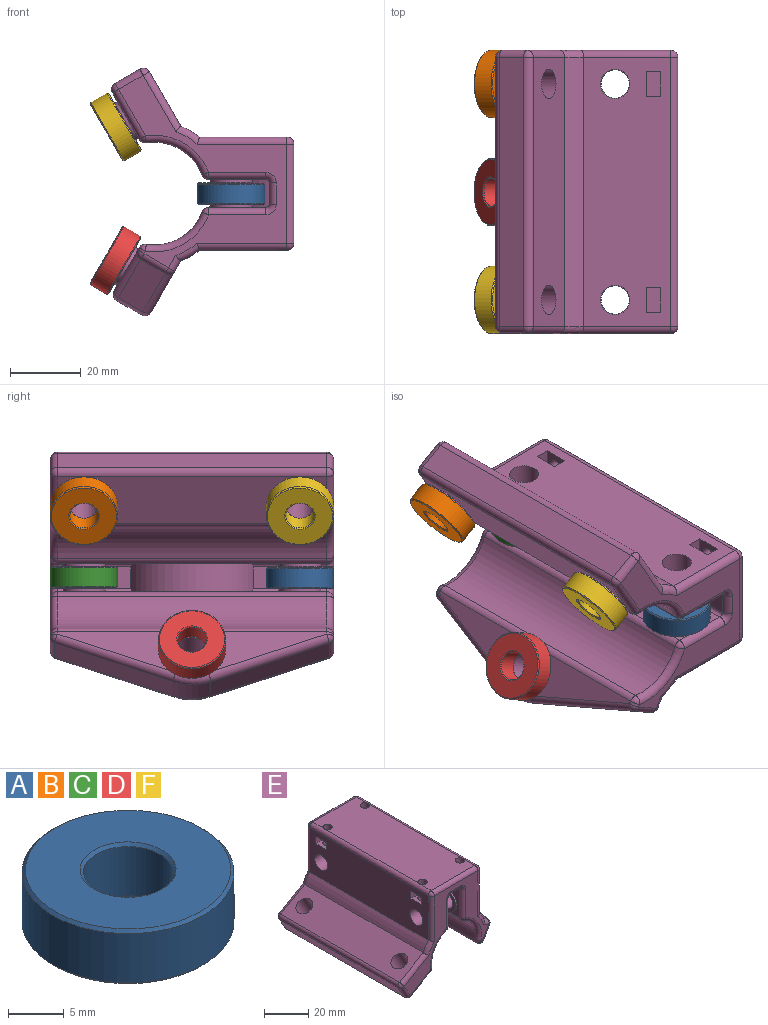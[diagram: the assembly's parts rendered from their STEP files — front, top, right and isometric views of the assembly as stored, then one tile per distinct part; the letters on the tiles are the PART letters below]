
ASSEMBLY  parts=6 mates=5
PART A: 8 faces, bbox 19x19x6 mm
  f0: cylinder r=4mm len=8mm, axis (0,0,-1), area 135.7mm2, adj f4,f6
  f1: cylinder r=9.5mm len=19mm, axis (0,0,-1), area 322.3mm2, adj f5,f7
  f2: plane 18.4x18.4mm, normal (0,0,1), area 207.8mm2, adj f6,f7
  f3: plane 18.4x18.4mm, normal (0,0,-1), area 207.8mm2, adj f4,f5
  f4: cone r=4.3mm half-angle=45deg, axis (0,0,-1), area 11.1mm2, adj f0,f3
  f5: cone r=9.5mm half-angle=45deg, axis (0,0,1), area 24.9mm2, adj f1,f3
  f6: cone r=4mm half-angle=45deg, axis (0,0,1), area 11.1mm2, adj f0,f2
  f7: cone r=9.2mm half-angle=45deg, axis (0,0,-1), area 24.9mm2, adj f1,f2
PART B: same geometry as A
PART C: same geometry as A
PART D: same geometry as A
PART E: 155 faces, bbox 70.9x80x51.6 mm
  f0: plane 54.37x47.54mm, normal (0,1,0), area 620.3mm2, adj f104,f108,f112,f114,f115,f117,f118,f119
  f1: plane 54.37x47.54mm, normal (0,-1,0), area 620.3mm2, adj f83,f84,f86,f87,f88,f89,f90,f91
  f2: plane 76x28mm, normal (0,0,1), area 2071.7mm2, adj f67,f68,f71,f74,f97,f124,f144,f147
  f3: plane 76x24.66mm, normal (-1,0,0), area 1712.3mm2, adj f14,f24,f25,f55,f56,f57,f58,f60
  f4: plane 76x24.71mm, normal (1,0,0), area 1716.4mm2, adj f13,f22,f23,f45,f46,f47,f48,f50
  f5: plane 20.76x6mm, normal (0,0,-1), area 124.5mm2, adj f6,f31,f32,f88
  f6: cylinder r=1mm len=21.18mm, axis (0,-1,0), area 32.8mm2, adj f5,f8,f32,f90
  f7: cylinder r=1mm len=21.18mm, axis (0,1,0), area 32.8mm2, adj f9,f17,f32,f119
  f8: plane 76x16.13mm, normal (1,0,0), area 738.4mm2, adj f6,f27,f30,f32,f41,f43,f92,f112
  f9: plane 76x16.13mm, normal (-1,0,0), area 738.4mm2, adj f7,f28,f31,f32,f37,f39,f84,f121
  f10: plane 76x15.34mm, normal (-0.5,0,0.87), area 1240.4mm2, adj f14,f20,f21,f105,f113,f118
  f11: plane 76x13.11mm, normal (0.5,0,-0.87), area 924.3mm2, adj f26,f33,f35,f100,f107,f108
  f12: plane 76x14.41mm, normal (0.5,0,0.87), area 734.6mm2, adj f13,f77,f91,f130,f134,f135,f136
  f13: cylinder r=20.5mm len=76mm, axis (0,1,0), area 472.9mm2, adj f4,f12,f93,f128
  f14: cylinder r=20.5mm len=76mm, axis (0,1,0), area 472.9mm2, adj f3,f10,f101,f120
  f15: plane 76x6.93mm, normal (-0.87,0,-0.5), area 608mm2, adj f106,f107,f113,f114
  f16: cylinder r=14.5mm len=76mm, axis (0,1,0), area 1486.2mm2, adj f26,f27,f96,f104
  f17: plane 20.76x6mm, normal (0,0,-1), area 124.5mm2, adj f7,f30,f32,f117
  f18: cylinder r=14.5mm len=76mm, axis (0,1,0), area 1489.3mm2, adj f28,f29,f83,f125
  f19: plane 76x12.21mm, normal (-0.5,0,-0.87), area 481.5mm2, adj f29,f78,f87,f129,f139,f140,f141
  f20: cylinder r=4.1mm len=15.36mm, axis (-0.5,0,0.87), area 334.9mm2, adj f10,f36
  f21: cylinder r=4.1mm len=15.36mm, axis (-0.5,0,0.87), area 334.9mm2, adj f10,f34
  f22: cylinder r=4.1mm len=12.85mm, axis (1,0,0), area 331mm2, adj f4,f40
  f23: cylinder r=4.1mm len=12.85mm, axis (1,0,0), area 331mm2, adj f4,f38
  f24: cylinder r=4.1mm len=12.85mm, axis (1,0,0), area 331mm2, adj f3,f44
  f25: cylinder r=4.1mm len=12.85mm, axis (1,0,0), area 331mm2, adj f3,f42
  f26: cylinder r=2mm len=76mm, axis (0,1,0), area 182mm2, adj f11,f16,f98,f103
  f27: cylinder r=2mm len=76mm, axis (0,1,0), area 182.2mm2, adj f8,f16,f94,f109
  f28: cylinder r=2mm len=76mm, axis (0,1,0), area 182.2mm2, adj f9,f18,f82,f123
  f29: cylinder r=2mm len=76mm, axis (0,1,0), area 182.4mm2, adj f18,f19,f85,f127
  f30: cylinder r=1mm len=21.18mm, axis (0,-1,0), area 32.8mm2, adj f8,f17,f32,f115
  f31: cylinder r=1mm len=21.18mm, axis (0,1,0), area 32.8mm2, adj f5,f9,f32,f86
  f32: cylinder r=18.5mm len=34.49mm, axis (1,0,0), area 354.4mm2, adj f5,f6,f7,f8,f9,f17,f30,f31
  f33: cylinder r=6mm len=12mm, axis (-0.5,0,0.87), area 37.7mm2, adj f11,f34
  f34: plane 12x10.39mm, normal (0.5,0,-0.87), area 60.3mm2, adj f21,f33
  f35: cylinder r=6mm len=12mm, axis (-0.5,0,0.87), area 37.7mm2, adj f11,f36
  f36: plane 12x10.39mm, normal (0.5,0,-0.87), area 60.3mm2, adj f20,f35
  f37: cylinder r=6mm len=12mm, axis (1,0,0), area 31.2mm2, adj f9,f38
  f38: plane 12x12mm, normal (-1,0,0), area 60.3mm2, adj f23,f37
  f39: cylinder r=6mm len=12mm, axis (1,0,0), area 31.2mm2, adj f9,f40
  f40: plane 12x12mm, normal (-1,0,0), area 60.3mm2, adj f22,f39
  f41: cylinder r=6mm len=12mm, axis (-1,0,0), area 32.9mm2, adj f8,f42
  f42: plane 12x12mm, normal (1,0,0), area 60.3mm2, adj f25,f41
  f43: cylinder r=6mm len=12mm, axis (-1,0,0), area 32.9mm2, adj f8,f44
  f44: plane 12x12mm, normal (1,0,0), area 60.3mm2, adj f24,f43
  f45: plane 8x4mm, normal (0,1,0), area 32mm2, adj f4,f46,f48,f49
  f46: plane 8x7mm, normal (0,0,1), area 41.8mm2, adj f4,f45,f47,f49,f75
  f47: plane 8x4mm, normal (0,-1,0), area 32mm2, adj f4,f46,f48,f49
  f48: plane 8x7mm, normal (0,0,-1), area 41.8mm2, adj f4,f45,f47,f49,f74
  f49: plane 7x4mm, normal (1,0,0), area 28mm2, adj f45,f46,f47,f48
  f50: plane 8x7mm, normal (0,0,1), area 41.8mm2, adj f4,f51,f53,f54,f72
  f51: plane 8x4mm, normal (0,-1,0), area 32mm2, adj f4,f50,f52,f54
  f52: plane 8x7mm, normal (0,0,-1), area 41.8mm2, adj f4,f51,f53,f54,f71
  f53: plane 8x4mm, normal (0,1,0), area 32mm2, adj f4,f50,f52,f54
  f54: plane 7x4mm, normal (1,0,0), area 28mm2, adj f50,f51,f52,f53
  f55: plane 8x7mm, normal (0,0,1), area 41.8mm2, adj f3,f56,f58,f59,f69
  f56: plane 8x4mm, normal (0,1,0), area 32mm2, adj f3,f55,f57,f59
  f57: plane 8x7mm, normal (0,0,-1), area 41.8mm2, adj f3,f56,f58,f59,f68
  f58: plane 8x4mm, normal (0,-1,0), area 32mm2, adj f3,f55,f57,f59
  f59: plane 7x4mm, normal (-1,0,0), area 28mm2, adj f55,f56,f57,f58
  f60: plane 8x7mm, normal (0,0,-1), area 41.8mm2, adj f3,f61,f63,f64,f67
  f61: plane 8x4mm, normal (0,-1,0), area 32mm2, adj f3,f60,f62,f64
  f62: plane 8x7mm, normal (0,0,1), area 41.8mm2, adj f3,f61,f63,f64,f66
  f63: plane 8x4mm, normal (0,1,0), area 32mm2, adj f3,f60,f62,f64
  f64: plane 7x4mm, normal (-1,0,0), area 28mm2, adj f60,f61,f62,f63
  f65: plane 4.25x4.25mm, normal (0,0,1), area 14.2mm2, adj f66
  f66: cylinder r=2.12mm len=4.25mm, axis (0,0,1), area 53.4mm2, adj f62,f65
  f67: cylinder r=2.12mm len=5mm, axis (0,0,1), area 66.8mm2, adj f2,f60,f147
  f68: cylinder r=2.12mm len=5mm, axis (0,0,1), area 66.8mm2, adj f2,f57,f147
  f69: cylinder r=2.12mm len=4.25mm, axis (0,0,1), area 53.4mm2, adj f55,f70
  f70: plane 4.25x4.25mm, normal (0,0,1), area 14.2mm2, adj f69
  f71: cylinder r=2.12mm len=5mm, axis (0,0,1), area 66.8mm2, adj f2,f52,f144
  f72: cylinder r=2.12mm len=4.25mm, axis (0,0,1), area 53.4mm2, adj f50,f73
  f73: plane 4.25x4.25mm, normal (0,0,1), area 14.2mm2, adj f72
  f74: cylinder r=2.12mm len=5mm, axis (0,0,1), area 66.8mm2, adj f2,f48,f144
  f75: cylinder r=2.12mm len=4.25mm, axis (0,0,1), area 53.4mm2, adj f46,f76
  f76: plane 4.25x4.25mm, normal (0,0,1), area 14.2mm2, adj f75
  f77: cylinder r=4.1mm len=15.36mm, axis (0.5,0,0.87), area 334.9mm2, adj f12,f79
  f78: cylinder r=6mm len=12mm, axis (0.5,0,0.87), area 37.7mm2, adj f19,f79
  f79: plane 12x10.39mm, normal (-0.5,0,-0.87), area 60.3mm2, adj f77,f78
  f80: plane 33.44x14.86mm, normal (0.81,-0.35,-0.47), area 285.7mm2, adj f89,f132,f134,f139
  f81: plane 33.44x14.86mm, normal (0.81,0.35,-0.47), area 285.7mm2, adj f131,f132,f136,f141
  f82: sphere r=2mm, area 4.8mm2, adj f28,f83,f84
  f83: torus R=16.5mm, axis (0,-1,0), area 64.6mm2, adj f1,f18,f82,f85
  f84: cylinder r=2mm len=16.13mm, axis (0,0,1), area 50.7mm2, adj f1,f9,f82,f86
  f85: sphere r=2mm, area 4.8mm2, adj f29,f83,f87
  f86: torus R=3mm, axis (0,-1,0), area 8.5mm2, adj f1,f31,f84,f88
  f87: cylinder r=2mm len=2.1mm, axis (-0.87,0,0.5), area 2.3mm2, adj f1,f19,f85,f138
  f88: cylinder r=2mm len=6mm, axis (-1,0,0), area 18.8mm2, adj f1,f5,f86,f90
  f89: cylinder r=2mm len=7.86mm, axis (-0.5,0,-0.87), area 19.4mm2, adj f1,f80,f133,f138
  f90: torus R=3mm, axis (0,-1,0), area 8.5mm2, adj f1,f6,f88,f92
  f91: cylinder r=2mm len=4.46mm, axis (0.87,0,-0.5), area 11.1mm2, adj f1,f12,f93,f133
  f92: cylinder r=2mm len=16.13mm, axis (0,0,-1), area 50.7mm2, adj f1,f8,f90,f94
  f93: torus R=18.5mm, axis (0,-1,0), area 20.4mm2, adj f1,f13,f91,f95
  f94: sphere r=2mm, area 4.8mm2, adj f27,f92,f96
  f95: cylinder r=2mm len=25.43mm, axis (0,0,-1), area 78.4mm2, adj f1,f4,f93,f145
  f96: torus R=16.5mm, axis (0,-1,0), area 64.5mm2, adj f1,f16,f94,f98
  f97: cylinder r=2mm len=28mm, axis (1,0,0), area 88mm2, adj f1,f2,f145,f148
  f98: sphere r=2mm, area 4.8mm2, adj f26,f96,f100
  f99: cylinder r=2mm len=25.38mm, axis (0,0,1), area 78.3mm2, adj f1,f3,f101,f148
  f100: cylinder r=2mm len=14.11mm, axis (-0.87,0,-0.5), area 47.6mm2, adj f1,f11,f98,f102
  f101: torus R=18.5mm, axis (0,-1,0), area 20.4mm2, adj f1,f14,f99,f105
  f102: sphere r=2mm, area 6.3mm2, adj f100,f106,f107
  f103: sphere r=2mm, area 4.8mm2, adj f26,f104,f108
  f104: torus R=16.5mm, axis (0,-1,0), area 64.5mm2, adj f0,f16,f103,f109
  f105: cylinder r=2mm len=16.96mm, axis (0.87,0,0.5), area 56.5mm2, adj f1,f10,f101,f110
  f106: cylinder r=2mm len=7.93mm, axis (-0.5,0,0.87), area 25.1mm2, adj f1,f15,f102,f110
  f107: cylinder r=2mm len=76mm, axis (0,1,0), area 238.8mm2, adj f11,f15,f102,f111
  f108: cylinder r=2mm len=14.11mm, axis (0.87,0,0.5), area 47.6mm2, adj f0,f11,f103,f111
  f109: sphere r=2mm, area 4.8mm2, adj f27,f104,f112
  f110: sphere r=2mm, area 6.3mm2, adj f105,f106,f113
  f111: sphere r=2mm, area 6.3mm2, adj f107,f108,f114
  f112: cylinder r=2mm len=16.13mm, axis (0,0,1), area 50.7mm2, adj f0,f8,f109,f115
  f113: cylinder r=2mm len=76mm, axis (0,1,0), area 238.8mm2, adj f10,f15,f110,f116
  f114: cylinder r=2mm len=7.93mm, axis (0.5,0,-0.87), area 25.1mm2, adj f0,f15,f111,f116
  f115: torus R=3mm, axis (0,-1,0), area 8.5mm2, adj f0,f30,f112,f117
  f116: sphere r=2mm, area 6.3mm2, adj f113,f114,f118
  f117: cylinder r=2mm len=6mm, axis (1,0,0), area 18.8mm2, adj f0,f17,f115,f119
  f118: cylinder r=2mm len=16.96mm, axis (-0.87,0,-0.5), area 56.5mm2, adj f0,f10,f116,f120
  f119: torus R=3mm, axis (0,-1,0), area 8.5mm2, adj f0,f7,f117,f121
  f120: torus R=18.5mm, axis (0,-1,0), area 20.4mm2, adj f0,f14,f118,f122
  f121: cylinder r=2mm len=16.13mm, axis (0,0,-1), area 50.7mm2, adj f0,f9,f119,f123
  f122: cylinder r=2mm len=25.38mm, axis (0,0,-1), area 78.3mm2, adj f0,f3,f120,f146
  f123: sphere r=2mm, area 4.8mm2, adj f28,f121,f125
  f124: cylinder r=2mm len=28mm, axis (-1,0,0), area 88mm2, adj f0,f2,f143,f146
  f125: torus R=16.5mm, axis (0,-1,0), area 64.6mm2, adj f0,f18,f123,f127
  f126: cylinder r=2mm len=25.43mm, axis (0,0,1), area 78.4mm2, adj f0,f4,f128,f143
  f127: sphere r=2mm, area 4.8mm2, adj f29,f125,f129
  f128: torus R=18.5mm, axis (0,-1,0), area 20.4mm2, adj f0,f13,f126,f130
  f129: cylinder r=2mm len=2.1mm, axis (0.87,0,-0.5), area 2.3mm2, adj f0,f19,f127,f142
  f130: cylinder r=2mm len=4.46mm, axis (-0.87,0,0.5), area 11.1mm2, adj f0,f12,f128,f137
  f131: cylinder r=2mm len=7.86mm, axis (0.5,0,0.87), area 19.4mm2, adj f0,f81,f137,f142
  f132: cylinder r=15mm len=10.53mm, axis (0.5,0,0.87), area 86.1mm2, adj f80,f81,f135,f140
  f133: sphere r=2mm, area 4.8mm2, adj f89,f91,f134
  f134: cylinder r=2mm len=34.14mm, axis (0.3,0.94,-0.18), area 112.2mm2, adj f12,f80,f133,f135
  f135: torus R=13mm, axis (0.5,0,0.87), area 32.2mm2, adj f12,f132,f134,f136
  f136: cylinder r=2mm len=34.14mm, axis (-0.3,0.94,0.18), area 112.2mm2, adj f12,f81,f135,f137
  f137: sphere r=2mm, area 4.8mm2, adj f130,f131,f136
  f138: sphere r=2mm, area 4.8mm2, adj f87,f89,f139
  f139: cylinder r=2mm len=34.14mm, axis (-0.3,-0.94,0.18), area 112.2mm2, adj f19,f80,f138,f140
  f140: torus R=13mm, axis (0.5,0,0.87), area 32.2mm2, adj f19,f132,f139,f141
  f141: cylinder r=2mm len=34.14mm, axis (0.3,-0.94,-0.18), area 112.2mm2, adj f19,f81,f140,f142
  f142: sphere r=2mm, area 4.8mm2, adj f129,f131,f141
  f143: sphere r=2mm, area 6.3mm2, adj f124,f126,f144
  f144: cylinder r=2mm len=76mm, axis (0,1,0), area 238.5mm2, adj f2,f4,f71,f74,f143,f145
  f145: sphere r=2mm, area 6.3mm2, adj f95,f97,f144
  f146: sphere r=2mm, area 6.3mm2, adj f122,f124,f147
  f147: cylinder r=2mm len=76mm, axis (0,1,0), area 238.5mm2, adj f2,f3,f67,f68,f146,f148
  f148: sphere r=2mm, area 6.3mm2, adj f97,f99,f147
  f149: cylinder r=12.5mm len=21.11mm, axis (1,0,0), area 200mm2, adj f150,f151,f152,f153,f154
  f150: cylinder r=1mm len=21.11mm, axis (0,1,0), area 32.4mm2, adj f149,f152,f153
  f151: cylinder r=1mm len=21.11mm, axis (0,-1,0), area 32.4mm2, adj f149,f152,f154
  f152: plane 21.11x6mm, normal (0,0,-1), area 126.6mm2, adj f149,f150,f151
  f153: plane 19.7x4.8mm, normal (-1,0,0), area 66mm2, adj f149,f150
  f154: plane 19.7x4.8mm, normal (1,0,0), area 66mm2, adj f149,f151
PART F: same geometry as A
PLACE A t=(5.17,-67.56,12.38)mm
PLACE B rot(axis=(0,1,0),60deg) t=(-30.04,-6.56,32.9)mm
PLACE C t=(5.17,-6.56,12.68)mm
PLACE D rot(axis=(0,1,0),120deg) t=(-30.1,-37.06,-1.82)mm
PLACE E rot(axis=(0,1,0),90deg) t=(-45.11,-37.06,80.44)mm
PLACE F rot(axis=(0,1,0),60deg) t=(-30.04,-67.56,32.9)mm
MATE fastened E.f22 <-> C.f1  axis (0,0,-1) through (5.17,-6.56,18.68)mm
MATE fastened E.f78 <-> D.f1  axis (0.87,0,-0.5) through (-24.9,-37.06,-4.82)mm
MATE fastened E.f33 <-> B.f1  axis (-0.87,0,-0.5) through (-24.84,-6.56,35.9)mm
MATE fastened E.f23 <-> A.f1  axis (0,0,1) through (5.17,-67.56,12.38)mm
MATE fastened E.f35 <-> F.f1  axis (-0.87,0,-0.5) through (-24.84,-67.56,35.9)mm
